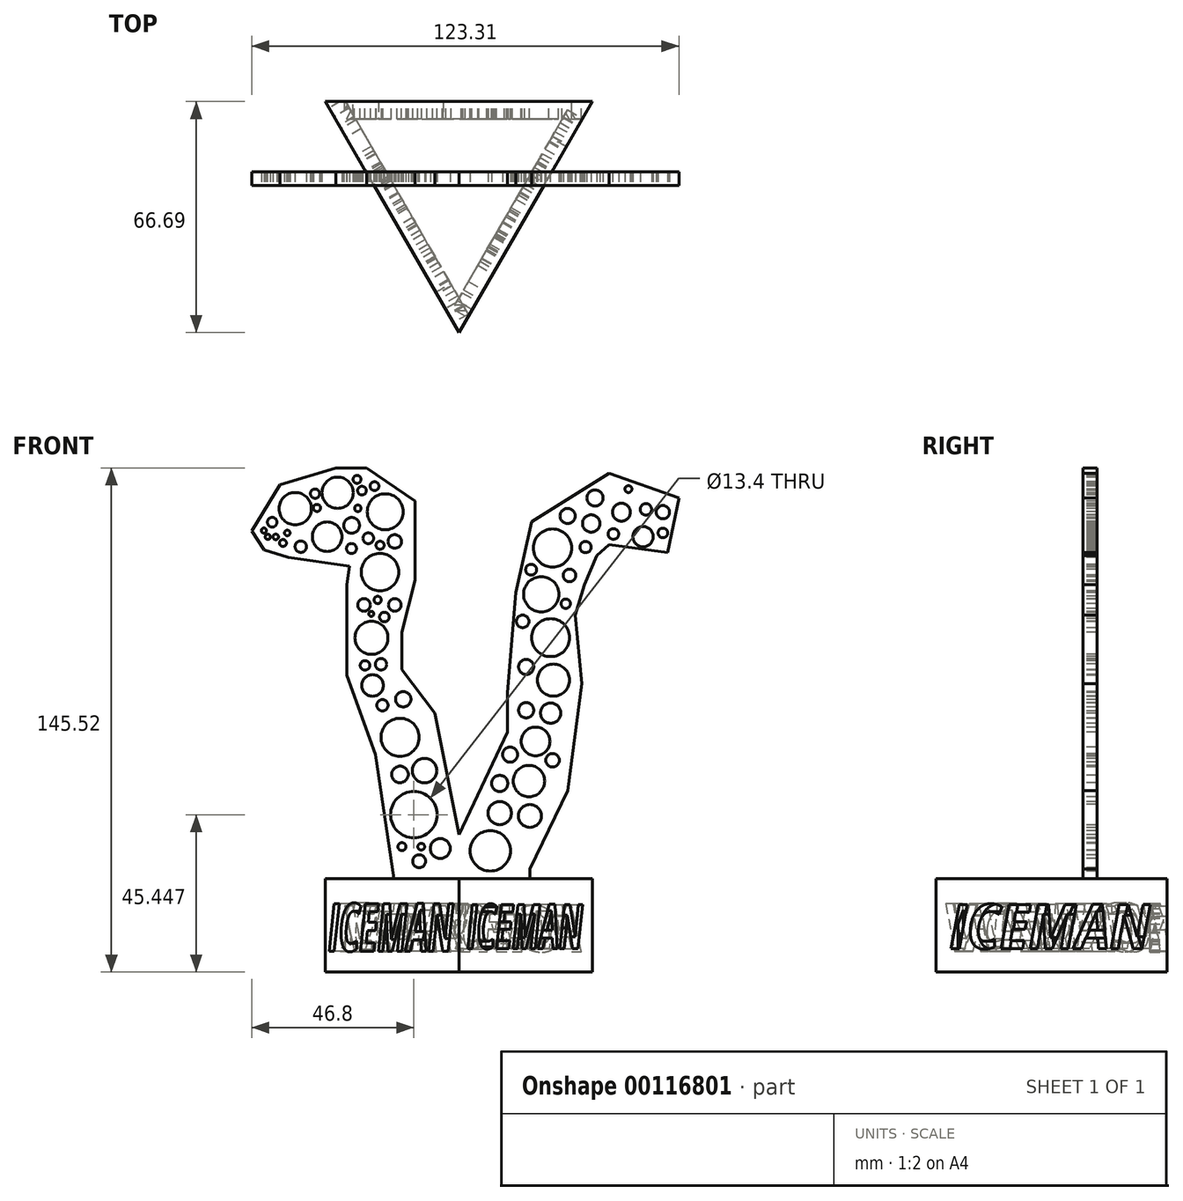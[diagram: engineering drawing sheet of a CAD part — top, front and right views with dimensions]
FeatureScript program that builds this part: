
annotation { "Feature Type Name" : "Feature", "Feature Type Description" : "" }
export const myFeature = defineFeature(function(context is Context, id is Id, definition is map)
    precondition{}
    {
        {
            var Q0;
            Q0=qCreatedBy(makeId("Top.planeOp"),FACE);
            var sketch = newSketch(context, id + "F0", { "sketchPlane" : qUnion([Q0])});
            skCircle(sketch, "E0.cCircle", {"center": v(0, 0) * mm, "radius": 22.23 * mm, "construction": true});
            skLineSegment(sketch, "E0.0", {"start": v(-38.5, 22.23) * mm, "end": v(38.5, 22.23) * mm});
            skLineSegment(sketch, "E0.1", {"start": v(38.5, 22.23) * mm, "end": v(0, -44.46) * mm});
            skLineSegment(sketch, "E0.2", {"start": v(0, -44.46) * mm, "end": v(-38.5, 22.23) * mm});
            skPoint(sketch, "E0.0.midPoint", {"position": v(0, 22.23) * mm});
            skSolve(sketch);
        }
        {
            var Q0;
            Q0 = qSketchRegion(id + "F0", true);
            extrude(context, id + "F1", {"entities" : qUnion([Q0]), "depth" : 27 * mm});
        }
        {
            var Q0;
            Q0=makeQuery(id+"F1.opExtrude","SWEPT_FACE",FACE,{"disambiguationData":[OSD([sQuery(id+"F0.wireOp",EDGE,"E0.0")])]});
            var sketch = newSketch(context, id + "F2", { "sketchPlane" : qUnion([Q0])});
            skText(sketch, "E1", { "text": "ICEMAN", "fontName": "OpenSans-BoldItalic.ttf"});
            skLineSegment(sketch, "E2", {"start": v(0, 35.53) * mm, "end": v(0, -12.2) * mm, "construction": true});
            skPoint(sketch, "E2.endSnap0", {"position": v(0, 27) * mm});
            const initialGuessF2  = {"E1": [-0.03582, 0.00594, 1, 0, 0.01323]};
            skSetInitialGuess(sketch, initialGuessF2);
            skSolve(sketch);
        }
        {
            var Q0;
            Q0 = qSketchRegion(id + "F2", true);
            extrude(context, id + "F3", {"entities" : qUnion([Q0]), "operationType" : NewBodyOperationType.REMOVE, "oppositeDirection" : true, "depth" : 5 * mm});
        }
        {
            var Q0;
            Q0=makeQuery(id+"F1.opExtrude","SWEPT_FACE",FACE,{"disambiguationData":[OSD([sQuery(id+"F0.wireOp",EDGE,"E0.1")])]});
            var sketch = newSketch(context, id + "F4", { "sketchPlane" : qUnion([Q0])});
            skText(sketch, "E3", { "text": "ICEMAN", "fontName": "OpenSans-BoldItalic.ttf"});
            const initialGuessF4  = {"E3": [-0.0339, 0.0068, 1, 0, 0.01285]};
            skSetInitialGuess(sketch, initialGuessF4);
            skSolve(sketch);
        }
        {
            var Q0;
            Q0 = qSketchRegion(id + "F4", true);
            extrude(context, id + "F5", {"entities" : qUnion([Q0]), "operationType" : NewBodyOperationType.REMOVE, "oppositeDirection" : true, "depth" : 5 * mm});
        }
        {
            var Q0;
            Q0=makeQuery(id+"F1.opExtrude","SWEPT_FACE",FACE,{"disambiguationData":[OSD([sQuery(id+"F0.wireOp",EDGE,"E0.2")])]});
            var sketch = newSketch(context, id + "F6", { "sketchPlane" : qUnion([Q0])});
            skText(sketch, "E4", { "text": "ICEMAN", "fontName": "OpenSans-BoldItalic.ttf"});
            const initialGuessF6  = {"E4": [-0.03687, 0.00604, 1, 0, 0.01387]};
            skSetInitialGuess(sketch, initialGuessF6);
            skSolve(sketch);
        }
        {
            var Q0;
            Q0 = qSketchRegion(id + "F6", true);
            var Q1;
            Q1 = qConstructionFilter(qBodyType(qCreatedBy(id + "F6" ,EDGE), BodyType.WIRE), ConstructionObject.NO);
            extrude(context, id + "F7", {"entities" : qUnion([Q0]), "operationType" : NewBodyOperationType.REMOVE, "surfaceEntities" : qUnion([Q1]), "oppositeDirection" : true, "depth" : 5 * mm});
        }
        {
            var Q0;
            Q0=makeQuery(id+"F1.opExtrude","CAP_FACE",FACE,{"disambiguationData":[OSD([sQuery(id+"F0.wireOp",EDGE,"E0.0"),sQuery(id+"F0.wireOp",EDGE,"E0.1"),sQuery(id+"F0.wireOp",EDGE,"E0.2")])],"isStart":false});
            var sketch = newSketch(context, id + "F8", { "sketchPlane" : qUnion([Q0])});
            skLineSegment(sketch, "E5.bottom", {"start": v(63.5, 2) * mm, "end": v(-63.5, 2) * mm});
            skLineSegment(sketch, "E5.top", {"start": v(63.5, -2) * mm, "end": v(-63.5, -2) * mm});
            skLineSegment(sketch, "E5.left", {"start": v(63.5, 2) * mm, "end": v(63.5, -2) * mm});
            skLineSegment(sketch, "E5.right", {"start": v(-63.5, 2) * mm, "end": v(-63.5, -2) * mm});
            skPoint(sketch, "E5.middle", {"position": v(0, 0) * mm});
            skSolve(sketch);
        }
        {
            var Q0;
            {var subQ0=sQuery(id+"F8.wireOp",EDGE,"E5.bottom");var subQ1=makeQuery(id+"F1.opExtrude","CAP_EDGE",EDGE,{"disambiguationData":[OSD([sQuery(id+"F0.wireOp",EDGE,"E0.1")])],"isStart":false});var subQ2=makeQuery(id+"F8.imprint","INTERSECT",VERTEX,{"derivedFrom":[subQ1,subQ0]});Q0=makeQuery(id+"F8.imprint","IMPRINT",FACE,{"disambiguationData":[TD([[makeQuery(id+"F8.imprint","IMPRINT",EDGE,{"disambiguationData":[TD([[subQ2,-1.0]])],"derivedFrom":subQ0}),1.0]])]});}
            var Q1;
            {var subQ0=sQuery(id+"F8.wireOp",EDGE,"E5.right");Q1=makeQuery(id+"F8.imprint","IMPRINT",FACE,{"disambiguationData":[TD([[makeQuery(id+"F8.imprint","IMPRINT",EDGE,{"derivedFrom":subQ0}),1.0]])]});}
            var Q2;
            {var subQ0=sQuery(id+"F8.wireOp",EDGE,"E5.left");Q2=makeQuery(id+"F8.imprint","IMPRINT",FACE,{"disambiguationData":[TD([[makeQuery(id+"F8.imprint","IMPRINT",EDGE,{"derivedFrom":subQ0}),-1.0]])]});}
            extrude(context, id + "F9", {"entities" : qUnion([Q0, Q1, Q2]), "operationType" : NewBodyOperationType.ADD, "depth" : 127 * mm});
        }
        {
            var Q0;
            Q0=makeQuery(id+"F9.opExtrude","SWEPT_FACE",FACE,{"disambiguationData":[OSD([sQuery(id+"F8.wireOp",EDGE,"E5.top")])]});
            var sketch = newSketch(context, id + "F10", { "sketchPlane" : qUnion([Q0])});
            skCircle(sketch, "E6", {"center": v(-50.78, 123.83) * mm, "radius": 1 * mm});
            skCircle(sketch, "E7", {"center": v(48.93, 139.4) * mm, "radius": 1 * mm});
            skCircle(sketch, "E8", {"center": v(-47.23, 133.75) * mm, "radius": 4.66 * mm});
            skCircle(sketch, "E9", {"center": v(-35, 138.33) * mm, "radius": 4.51 * mm});
            skCircle(sketch, "E10", {"center": v(-21.26, 132.83) * mm, "radius": 5.2 * mm});
            skCircle(sketch, "E11", {"center": v(-22.79, 115.42) * mm, "radius": 5.4 * mm});
            skCircle(sketch, "E12", {"center": v(-25.23, 96.47) * mm, "radius": 4.77 * mm});
            skCircle(sketch, "E13", {"center": v(-16.98, 67.75) * mm, "radius": 5.5 * mm});
            skCircle(sketch, "E14", {"center": v(-13.01, 45.45) * mm, "radius": 6.7 * mm});
            skCircle(sketch, "E15", {"center": v(-5.37, 35.67) * mm, "radius": 2.88 * mm});
            skCircle(sketch, "E16", {"center": v(-11.48, 32) * mm, "radius": 1.86 * mm});
            skCircle(sketch, "E17", {"center": v(-16.98, 57.06) * mm, "radius": 2.39 * mm});
            skCircle(sketch, "E18", {"center": v(-16.07, 78.75) * mm, "radius": 2.22 * mm});
            skCircle(sketch, "E19", {"center": v(-24.93, 82.72) * mm, "radius": 3.12 * mm});
            skCircle(sketch, "E20", {"center": v(-27.37, 105.95) * mm, "radius": 1.83 * mm});
            skCircle(sketch, "E21", {"center": v(-18.51, 105.95) * mm, "radius": 1.83 * mm});
            skCircle(sketch, "E22", {"center": v(-22.48, 88.83) * mm, "radius": 1.65 * mm});
            skCircle(sketch, "E23", {"center": v(-26.15, 125.2) * mm, "radius": 1.56 * mm});
            skCircle(sketch, "E24", {"center": v(-18.51, 124.28) * mm, "radius": 1.96 * mm});
            skCircle(sketch, "E25", {"center": v(-27.98, 138.94) * mm, "radius": 1.26 * mm});
            skCircle(sketch, "E26", {"center": v(-29.16, 133.83) * mm, "radius": 0.94 * mm});
            skCircle(sketch, "E27", {"center": v(-40.95, 133.95) * mm, "radius": 1.04 * mm});
            skCircle(sketch, "E28", {"center": v(-41.52, 138.07) * mm, "radius": 1.34 * mm});
            skCircle(sketch, "E29", {"center": v(-53.89, 129.83) * mm, "radius": 1.4 * mm});
            skCircle(sketch, "E30", {"center": v(-49.54, 126.74) * mm, "radius": 0.8 * mm});
            skCircle(sketch, "E31", {"center": v(-55.14, 125.6) * mm, "radius": 0.77 * mm});
            skCircle(sketch, "E32", {"center": v(-52.86, 125.6) * mm, "radius": 0.8 * mm});
            skCircle(sketch, "E33", {"center": v(-56.29, 127.42) * mm, "radius": 0.73 * mm});
            skCircle(sketch, "E34", {"center": v(-24.36, 140.24) * mm, "radius": 1.28 * mm});
            skCircle(sketch, "E35", {"center": v(-29.4, 142.19) * mm, "radius": 1.14 * mm});
            skCircle(sketch, "E36", {"center": v(-22.76, 123.19) * mm, "radius": 1.18 * mm});
            skCircle(sketch, "E37", {"center": v(-23.44, 107.4) * mm, "radius": 1.06 * mm});
            skCircle(sketch, "E38", {"center": v(-21.5, 102.47) * mm, "radius": 1.4 * mm});
            skCircle(sketch, "E39", {"center": v(-25.27, 103.39) * mm, "radius": 0.73 * mm});
            skCircle(sketch, "E40", {"center": v(-27.1, 88.5) * mm, "radius": 1.38 * mm});
            skCircle(sketch, "E41", {"center": v(-22.07, 77.01) * mm, "radius": 1.63 * mm});
            skCircle(sketch, "E42", {"center": v(-9.9, 58.14) * mm, "radius": 3.54 * mm});
            skCircle(sketch, "E43", {"center": v(-16.45, 36.2) * mm, "radius": 1.15 * mm});
            skCircle(sketch, "E44", {"center": v(-10.86, 36.2) * mm, "radius": 0.98 * mm});
            skCircle(sketch, "E45", {"center": v(9.06, 35) * mm, "radius": 5.82 * mm});
            skCircle(sketch, "E46", {"center": v(11.79, 45.89) * mm, "radius": 3.37 * mm});
            skCircle(sketch, "E47", {"center": v(20.5, 45.07) * mm, "radius": 3.31 * mm});
            skCircle(sketch, "E48", {"center": v(20.22, 55.14) * mm, "radius": 4.53 * mm});
            skCircle(sketch, "E49", {"center": v(22.13, 66.58) * mm, "radius": 4.15 * mm});
            skCircle(sketch, "E50", {"center": v(26.49, 74.74) * mm, "radius": 2.93 * mm});
            skCircle(sketch, "E51", {"center": v(27.3, 84.27) * mm, "radius": 4.64 * mm});
            skCircle(sketch, "E52", {"center": v(26.49, 96.52) * mm, "radius": 5.47 * mm});
            skCircle(sketch, "E53", {"center": v(19.4, 75.56) * mm, "radius": 2.2 * mm});
            skCircle(sketch, "E54", {"center": v(19.4, 88.08) * mm, "radius": 2.18 * mm});
            skCircle(sketch, "E55", {"center": v(23.76, 109.04) * mm, "radius": 5.09 * mm});
            skCircle(sketch, "E56", {"center": v(27.03, 122.38) * mm, "radius": 5.51 * mm});
            skCircle(sketch, "E57", {"center": v(38.2, 129.46) * mm, "radius": 2.5 * mm});
            skCircle(sketch, "E58", {"center": v(31.39, 131.64) * mm, "radius": 2.2 * mm});
            skCircle(sketch, "E59", {"center": v(39.28, 136.8) * mm, "radius": 2.34 * mm});
            skCircle(sketch, "E60", {"center": v(46.9, 132.72) * mm, "radius": 2.58 * mm});
            skCircle(sketch, "E61", {"center": v(53.16, 125.65) * mm, "radius": 2.93 * mm});
            skCircle(sketch, "E62", {"center": v(53.98, 133.54) * mm, "radius": 1.66 * mm});
            skCircle(sketch, "E63", {"center": v(58.88, 132.72) * mm, "radius": 1.92 * mm});
            skCircle(sketch, "E64", {"center": v(58.88, 126.74) * mm, "radius": 1.39 * mm});
            skCircle(sketch, "E65", {"center": v(31.93, 114.49) * mm, "radius": 1.83 * mm});
            skCircle(sketch, "E66", {"center": v(30.84, 106.32) * mm, "radius": 1.36 * mm});
            skCircle(sketch, "E67", {"center": v(36.56, 122.65) * mm, "radius": 1.63 * mm});
            skLineSegment(sketch, "E68", {"start": v(0, 39.63) * mm, "end": v(-7, 74.74) * mm});
            skLineSegment(sketch, "E69", {"start": v(-7, 74.74) * mm, "end": v(-16.52, 87.27) * mm});
            skLineSegment(sketch, "E70", {"start": v(-16.52, 87.27) * mm, "end": v(-16.52, 98.15) * mm});
            skLineSegment(sketch, "E71", {"start": v(-16.52, 98.15) * mm, "end": v(-12.71, 113.13) * mm});
            skLineSegment(sketch, "E72", {"start": v(-12.71, 113.13) * mm, "end": v(-12.71, 136) * mm});
            skLineSegment(sketch, "E73", {"start": v(-12.71, 136) * mm, "end": v(-26.6, 145.52) * mm});
            skLineSegment(sketch, "E74", {"start": v(-26.6, 145.52) * mm, "end": v(-35.58, 145.52) * mm});
            skLineSegment(sketch, "E75", {"start": v(-35.58, 145.52) * mm, "end": v(-51.64, 140.62) * mm});
            skLineSegment(sketch, "E76", {"start": v(-51.64, 140.62) * mm, "end": v(-59.8, 127.28) * mm});
            skLineSegment(sketch, "E77", {"start": v(-59.8, 127.28) * mm, "end": v(-56.27, 121.84) * mm});
            skLineSegment(sketch, "E78", {"start": v(-56.27, 121.84) * mm, "end": v(-49.19, 119.66) * mm});
            skLineSegment(sketch, "E79", {"start": v(-31.54, 117.1) * mm, "end": v(-32.31, 111.76) * mm});
            skLineSegment(sketch, "E80", {"start": v(-32.31, 111.76) * mm, "end": v(-32.31, 85.63) * mm});
            skLineSegment(sketch, "E81", {"start": v(-32.31, 85.63) * mm, "end": v(-24.15, 62.77) * mm});
            skLineSegment(sketch, "E82", {"start": v(-24.15, 62.77) * mm, "end": v(-18.7, 27) * mm});
            skLineSegment(sketch, "E83", {"start": v(0, 39.63) * mm, "end": v(14.01, 69.28) * mm});
            skLineSegment(sketch, "E84", {"start": v(14.01, 69.28) * mm, "end": v(14.01, 80.73) * mm});
            skLineSegment(sketch, "E85", {"start": v(14.01, 80.73) * mm, "end": v(16.41, 109.59) * mm});
            skLineSegment(sketch, "E86", {"start": v(16.41, 109.59) * mm, "end": v(21.04, 130) * mm});
            skLineSegment(sketch, "E87", {"start": v(21.04, 130) * mm, "end": v(43.36, 143.89) * mm});
            skLineSegment(sketch, "E88", {"start": v(43.36, 143.89) * mm, "end": v(63.5, 136.8) * mm});
            skLineSegment(sketch, "E89", {"start": v(63.5, 136.8) * mm, "end": v(60.24, 121.02) * mm});
            skLineSegment(sketch, "E90", {"start": v(60.24, 121.02) * mm, "end": v(43.34, 123.36) * mm});
            skLineSegment(sketch, "E91", {"start": v(43.34, 123.36) * mm, "end": v(39.82, 120.2) * mm});
            skLineSegment(sketch, "E92", {"start": v(39.82, 120.2) * mm, "end": v(36.29, 111.76) * mm});
            skLineSegment(sketch, "E93", {"start": v(36.29, 111.76) * mm, "end": v(33.56, 103.05) * mm});
            skLineSegment(sketch, "E94", {"start": v(33.56, 103.05) * mm, "end": v(35.47, 83.18) * mm});
            skLineSegment(sketch, "E95", {"start": v(35.47, 83.18) * mm, "end": v(31.39, 52.42) * mm});
            skLineSegment(sketch, "E96", {"start": v(31.39, 52.42) * mm, "end": v(20.5, 29.83) * mm});
            skCircle(sketch, "E97", {"center": v(11.79, 54.45) * mm, "radius": 2.34 * mm});
            skPoint(sketch, "E97.centerSnap0", {"position": v(7, 54.45) * mm});
            skCircle(sketch, "E98", {"center": v(14.78, 62.77) * mm, "radius": 2.18 * mm});
            skCircle(sketch, "E99", {"center": v(27.03, 61.13) * mm, "radius": 1.96 * mm});
            skLineSegment(sketch, "E100", {"start": v(-49.19, 119.66) * mm, "end": v(-31.54, 117.1) * mm});
            skCircle(sketch, "E101", {"center": v(-38.03, 125.65) * mm, "radius": 4.26 * mm});
            skCircle(sketch, "E102", {"center": v(-30.95, 128.91) * mm, "radius": 2.27 * mm});
            skCircle(sketch, "E103", {"center": v(-31, 122.23) * mm, "radius": 1.45 * mm});
            skCircle(sketch, "E104", {"center": v(-45.63, 122.77) * mm, "radius": 1.65 * mm});
            skCircle(sketch, "E105", {"center": v(20.84, 116.12) * mm, "radius": 1.58 * mm});
            skCircle(sketch, "E106", {"center": v(18.41, 101.2) * mm, "radius": 1.82 * mm});
            skCircle(sketch, "E107", {"center": v(44.6, 126.43) * mm, "radius": 1.53 * mm});
            skLineSegment(sketch, "E108", {"start": v(20.5, 29.83) * mm, "end": v(20.5, 27) * mm});
            skPoint(sketch, "E108.endSnap0", {"position": v(0, 27) * mm});
            skSolve(sketch);
        }
        {
            var Q0;
            Q0=makeQuery(id+"F10.imprint","IMPRINT",FACE,{"disambiguationData":[TD([[makeQuery(id+"F10.imprint","IMPRINT",EDGE,{"derivedFrom":sQuery(id+"F10.wireOp",EDGE,"E68")}),-1.0]])]});
            var Q1;
            {var subQ13=sQuery(id+"F10.wireOp",EDGE,"E89");Q1=makeQuery(id+"F10.imprint","IMPRINT",FACE,{"disambiguationData":[TD([[makeQuery(id+"F10.imprint","IMPRINT",EDGE,{"derivedFrom":subQ13}),1.0]])]});}
            var Q2;
            Q2=makeQuery(id+"F10.imprint","IMPRINT",FACE,{"disambiguationData":[TD([[makeQuery(id+"F10.imprint","IMPRINT",EDGE,{"derivedFrom":sQuery(id+"F10.wireOp",EDGE,"E101")}),1.0]])]});
            var Q3;
            Q3=makeQuery(id+"F10.imprint","IMPRINT",FACE,{"disambiguationData":[TD([[makeQuery(id+"F10.imprint","IMPRINT",EDGE,{"derivedFrom":sQuery(id+"F10.wireOp",EDGE,"E11")}),1.0]])]});
            var Q4;
            Q4=makeQuery(id+"F10.imprint","IMPRINT",FACE,{"disambiguationData":[TD([[makeQuery(id+"F10.imprint","IMPRINT",EDGE,{"derivedFrom":sQuery(id+"F10.wireOp",EDGE,"E9")}),1.0]])]});
            var Q5;
            Q5=makeQuery(id+"F10.imprint","IMPRINT",FACE,{"disambiguationData":[TD([[makeQuery(id+"F10.imprint","IMPRINT",EDGE,{"derivedFrom":sQuery(id+"F10.wireOp",EDGE,"E8")}),1.0]])]});
            var Q6;
            Q6=makeQuery(id+"F10.imprint","IMPRINT",FACE,{"disambiguationData":[TD([[makeQuery(id+"F10.imprint","IMPRINT",EDGE,{"derivedFrom":sQuery(id+"F10.wireOp",EDGE,"E29")}),1.0]])]});
            var Q7;
            Q7=makeQuery(id+"F10.imprint","IMPRINT",FACE,{"disambiguationData":[TD([[makeQuery(id+"F10.imprint","IMPRINT",EDGE,{"derivedFrom":sQuery(id+"F10.wireOp",EDGE,"E33")}),1.0]])]});
            var Q8;
            Q8=makeQuery(id+"F10.imprint","IMPRINT",FACE,{"disambiguationData":[TD([[makeQuery(id+"F10.imprint","IMPRINT",EDGE,{"derivedFrom":sQuery(id+"F10.wireOp",EDGE,"E31")}),1.0]])]});
            var Q9;
            Q9=makeQuery(id+"F10.imprint","IMPRINT",FACE,{"disambiguationData":[TD([[makeQuery(id+"F10.imprint","IMPRINT",EDGE,{"derivedFrom":sQuery(id+"F10.wireOp",EDGE,"E32")}),1.0]])]});
            var Q10;
            Q10=makeQuery(id+"F10.imprint","IMPRINT",FACE,{"disambiguationData":[TD([[makeQuery(id+"F10.imprint","IMPRINT",EDGE,{"derivedFrom":sQuery(id+"F10.wireOp",EDGE,"E6")}),1.0]])]});
            var Q11;
            Q11=makeQuery(id+"F10.imprint","IMPRINT",FACE,{"disambiguationData":[TD([[makeQuery(id+"F10.imprint","IMPRINT",EDGE,{"derivedFrom":sQuery(id+"F10.wireOp",EDGE,"E30")}),1.0]])]});
            var Q12;
            Q12=makeQuery(id+"F10.imprint","IMPRINT",FACE,{"disambiguationData":[TD([[makeQuery(id+"F10.imprint","IMPRINT",EDGE,{"derivedFrom":sQuery(id+"F10.wireOp",EDGE,"E104")}),1.0]])]});
            var Q13;
            Q13=makeQuery(id+"F10.imprint","IMPRINT",FACE,{"disambiguationData":[TD([[makeQuery(id+"F10.imprint","IMPRINT",EDGE,{"derivedFrom":sQuery(id+"F10.wireOp",EDGE,"E102")}),1.0]])]});
            var Q14;
            Q14=makeQuery(id+"F10.imprint","IMPRINT",FACE,{"disambiguationData":[TD([[makeQuery(id+"F10.imprint","IMPRINT",EDGE,{"derivedFrom":sQuery(id+"F10.wireOp",EDGE,"E27")}),1.0]])]});
            var Q15;
            Q15=makeQuery(id+"F10.imprint","IMPRINT",FACE,{"disambiguationData":[TD([[makeQuery(id+"F10.imprint","IMPRINT",EDGE,{"derivedFrom":sQuery(id+"F10.wireOp",EDGE,"E28")}),1.0]])]});
            var Q16;
            Q16=makeQuery(id+"F10.imprint","IMPRINT",FACE,{"disambiguationData":[TD([[makeQuery(id+"F10.imprint","IMPRINT",EDGE,{"derivedFrom":sQuery(id+"F10.wireOp",EDGE,"E10")}),1.0]])]});
            var Q17;
            Q17=makeQuery(id+"F10.imprint","IMPRINT",FACE,{"disambiguationData":[TD([[makeQuery(id+"F10.imprint","IMPRINT",EDGE,{"derivedFrom":sQuery(id+"F10.wireOp",EDGE,"E26")}),1.0]])]});
            var Q18;
            Q18=makeQuery(id+"F10.imprint","IMPRINT",FACE,{"disambiguationData":[TD([[makeQuery(id+"F10.imprint","IMPRINT",EDGE,{"derivedFrom":sQuery(id+"F10.wireOp",EDGE,"E23")}),1.0]])]});
            var Q19;
            Q19=makeQuery(id+"F10.imprint","IMPRINT",FACE,{"disambiguationData":[TD([[makeQuery(id+"F10.imprint","IMPRINT",EDGE,{"derivedFrom":sQuery(id+"F10.wireOp",EDGE,"E103")}),1.0]])]});
            var Q20;
            Q20=makeQuery(id+"F10.imprint","IMPRINT",FACE,{"disambiguationData":[TD([[makeQuery(id+"F10.imprint","IMPRINT",EDGE,{"derivedFrom":sQuery(id+"F10.wireOp",EDGE,"E36")}),1.0]])]});
            var Q21;
            Q21=makeQuery(id+"F10.imprint","IMPRINT",FACE,{"disambiguationData":[TD([[makeQuery(id+"F10.imprint","IMPRINT",EDGE,{"derivedFrom":sQuery(id+"F10.wireOp",EDGE,"E24")}),1.0]])]});
            var Q22;
            Q22=makeQuery(id+"F10.imprint","IMPRINT",FACE,{"disambiguationData":[TD([[makeQuery(id+"F10.imprint","IMPRINT",EDGE,{"derivedFrom":sQuery(id+"F10.wireOp",EDGE,"E37")}),1.0]])]});
            var Q23;
            Q23=makeQuery(id+"F10.imprint","IMPRINT",FACE,{"disambiguationData":[TD([[makeQuery(id+"F10.imprint","IMPRINT",EDGE,{"derivedFrom":sQuery(id+"F10.wireOp",EDGE,"E20")}),1.0]])]});
            var Q24;
            Q24=makeQuery(id+"F10.imprint","IMPRINT",FACE,{"disambiguationData":[TD([[makeQuery(id+"F10.imprint","IMPRINT",EDGE,{"derivedFrom":sQuery(id+"F10.wireOp",EDGE,"E39")}),1.0]])]});
            var Q25;
            Q25=makeQuery(id+"F10.imprint","IMPRINT",FACE,{"disambiguationData":[TD([[makeQuery(id+"F10.imprint","IMPRINT",EDGE,{"derivedFrom":sQuery(id+"F10.wireOp",EDGE,"E38")}),1.0]])]});
            var Q26;
            Q26=makeQuery(id+"F10.imprint","IMPRINT",FACE,{"disambiguationData":[TD([[makeQuery(id+"F10.imprint","IMPRINT",EDGE,{"derivedFrom":sQuery(id+"F10.wireOp",EDGE,"E21")}),1.0]])]});
            var Q27;
            Q27=makeQuery(id+"F10.imprint","IMPRINT",FACE,{"disambiguationData":[TD([[makeQuery(id+"F10.imprint","IMPRINT",EDGE,{"derivedFrom":sQuery(id+"F10.wireOp",EDGE,"E12")}),1.0]])]});
            var Q28;
            Q28=makeQuery(id+"F10.imprint","IMPRINT",FACE,{"disambiguationData":[TD([[makeQuery(id+"F10.imprint","IMPRINT",EDGE,{"derivedFrom":sQuery(id+"F10.wireOp",EDGE,"E40")}),1.0]])]});
            var Q29;
            Q29=makeQuery(id+"F10.imprint","IMPRINT",FACE,{"disambiguationData":[TD([[makeQuery(id+"F10.imprint","IMPRINT",EDGE,{"derivedFrom":sQuery(id+"F10.wireOp",EDGE,"E22")}),1.0]])]});
            var Q30;
            Q30=makeQuery(id+"F10.imprint","IMPRINT",FACE,{"disambiguationData":[TD([[makeQuery(id+"F10.imprint","IMPRINT",EDGE,{"derivedFrom":sQuery(id+"F10.wireOp",EDGE,"E19")}),1.0]])]});
            var Q31;
            Q31=makeQuery(id+"F10.imprint","IMPRINT",FACE,{"disambiguationData":[TD([[makeQuery(id+"F10.imprint","IMPRINT",EDGE,{"derivedFrom":sQuery(id+"F10.wireOp",EDGE,"E41")}),1.0]])]});
            var Q32;
            Q32=makeQuery(id+"F10.imprint","IMPRINT",FACE,{"disambiguationData":[TD([[makeQuery(id+"F10.imprint","IMPRINT",EDGE,{"derivedFrom":sQuery(id+"F10.wireOp",EDGE,"E18")}),1.0]])]});
            var Q33;
            Q33=makeQuery(id+"F10.imprint","IMPRINT",FACE,{"disambiguationData":[TD([[makeQuery(id+"F10.imprint","IMPRINT",EDGE,{"derivedFrom":sQuery(id+"F10.wireOp",EDGE,"E13")}),1.0]])]});
            var Q34;
            Q34=makeQuery(id+"F10.imprint","IMPRINT",FACE,{"disambiguationData":[TD([[makeQuery(id+"F10.imprint","IMPRINT",EDGE,{"derivedFrom":sQuery(id+"F10.wireOp",EDGE,"E63")}),1.0]])]});
            var Q35;
            Q35=makeQuery(id+"F10.imprint","IMPRINT",FACE,{"disambiguationData":[TD([[makeQuery(id+"F10.imprint","IMPRINT",EDGE,{"derivedFrom":sQuery(id+"F10.wireOp",EDGE,"E60")}),1.0]])]});
            var Q36;
            Q36=makeQuery(id+"F10.imprint","IMPRINT",FACE,{"disambiguationData":[TD([[makeQuery(id+"F10.imprint","IMPRINT",EDGE,{"derivedFrom":sQuery(id+"F10.wireOp",EDGE,"E107")}),1.0]])]});
            var Q37;
            Q37=makeQuery(id+"F10.imprint","IMPRINT",FACE,{"disambiguationData":[TD([[makeQuery(id+"F10.imprint","IMPRINT",EDGE,{"derivedFrom":sQuery(id+"F10.wireOp",EDGE,"E57")}),1.0]])]});
            var Q38;
            Q38=makeQuery(id+"F10.imprint","IMPRINT",FACE,{"disambiguationData":[TD([[makeQuery(id+"F10.imprint","IMPRINT",EDGE,{"derivedFrom":sQuery(id+"F10.wireOp",EDGE,"E58")}),1.0]])]});
            var Q39;
            Q39=makeQuery(id+"F10.imprint","IMPRINT",FACE,{"disambiguationData":[TD([[makeQuery(id+"F10.imprint","IMPRINT",EDGE,{"derivedFrom":sQuery(id+"F10.wireOp",EDGE,"E56")}),1.0]])]});
            var Q40;
            Q40=makeQuery(id+"F10.imprint","IMPRINT",FACE,{"disambiguationData":[TD([[makeQuery(id+"F10.imprint","IMPRINT",EDGE,{"derivedFrom":sQuery(id+"F10.wireOp",EDGE,"E55")}),1.0]])]});
            var Q41;
            Q41=makeQuery(id+"F10.imprint","IMPRINT",FACE,{"disambiguationData":[TD([[makeQuery(id+"F10.imprint","IMPRINT",EDGE,{"derivedFrom":sQuery(id+"F10.wireOp",EDGE,"E105")}),1.0]])]});
            var Q42;
            Q42=makeQuery(id+"F10.imprint","IMPRINT",FACE,{"disambiguationData":[TD([[makeQuery(id+"F10.imprint","IMPRINT",EDGE,{"derivedFrom":sQuery(id+"F10.wireOp",EDGE,"E106")}),1.0]])]});
            var Q43;
            Q43=makeQuery(id+"F10.imprint","IMPRINT",FACE,{"disambiguationData":[TD([[makeQuery(id+"F10.imprint","IMPRINT",EDGE,{"derivedFrom":sQuery(id+"F10.wireOp",EDGE,"E66")}),1.0]])]});
            var Q44;
            Q44=makeQuery(id+"F10.imprint","IMPRINT",FACE,{"disambiguationData":[TD([[makeQuery(id+"F10.imprint","IMPRINT",EDGE,{"derivedFrom":sQuery(id+"F10.wireOp",EDGE,"E65")}),1.0]])]});
            var Q45;
            Q45=makeQuery(id+"F10.imprint","IMPRINT",FACE,{"disambiguationData":[TD([[makeQuery(id+"F10.imprint","IMPRINT",EDGE,{"derivedFrom":sQuery(id+"F10.wireOp",EDGE,"E52")}),1.0]])]});
            var Q46;
            Q46=makeQuery(id+"F10.imprint","IMPRINT",FACE,{"disambiguationData":[TD([[makeQuery(id+"F10.imprint","IMPRINT",EDGE,{"derivedFrom":sQuery(id+"F10.wireOp",EDGE,"E51")}),1.0]])]});
            var Q47;
            Q47=makeQuery(id+"F10.imprint","IMPRINT",FACE,{"disambiguationData":[TD([[makeQuery(id+"F10.imprint","IMPRINT",EDGE,{"derivedFrom":sQuery(id+"F10.wireOp",EDGE,"E54")}),1.0]])]});
            var Q48;
            Q48=makeQuery(id+"F10.imprint","IMPRINT",FACE,{"disambiguationData":[TD([[makeQuery(id+"F10.imprint","IMPRINT",EDGE,{"derivedFrom":sQuery(id+"F10.wireOp",EDGE,"E53")}),1.0]])]});
            var Q49;
            Q49=makeQuery(id+"F10.imprint","IMPRINT",FACE,{"disambiguationData":[TD([[makeQuery(id+"F10.imprint","IMPRINT",EDGE,{"derivedFrom":sQuery(id+"F10.wireOp",EDGE,"E50")}),1.0]])]});
            var Q50;
            Q50=makeQuery(id+"F10.imprint","IMPRINT",FACE,{"disambiguationData":[TD([[makeQuery(id+"F10.imprint","IMPRINT",EDGE,{"derivedFrom":sQuery(id+"F10.wireOp",EDGE,"E49")}),1.0]])]});
            var Q51;
            Q51=makeQuery(id+"F10.imprint","IMPRINT",FACE,{"disambiguationData":[TD([[makeQuery(id+"F10.imprint","IMPRINT",EDGE,{"derivedFrom":sQuery(id+"F10.wireOp",EDGE,"E98")}),1.0]])]});
            var Q52;
            Q52=makeQuery(id+"F10.imprint","IMPRINT",FACE,{"disambiguationData":[TD([[makeQuery(id+"F10.imprint","IMPRINT",EDGE,{"derivedFrom":sQuery(id+"F10.wireOp",EDGE,"E48")}),1.0]])]});
            var Q53;
            Q53=makeQuery(id+"F10.imprint","IMPRINT",FACE,{"disambiguationData":[TD([[makeQuery(id+"F10.imprint","IMPRINT",EDGE,{"derivedFrom":sQuery(id+"F10.wireOp",EDGE,"E99")}),1.0]])]});
            var Q54;
            Q54=makeQuery(id+"F10.imprint","IMPRINT",FACE,{"disambiguationData":[TD([[makeQuery(id+"F10.imprint","IMPRINT",EDGE,{"derivedFrom":sQuery(id+"F10.wireOp",EDGE,"E47")}),1.0]])]});
            var Q55;
            Q55=makeQuery(id+"F10.imprint","IMPRINT",FACE,{"disambiguationData":[TD([[makeQuery(id+"F10.imprint","IMPRINT",EDGE,{"derivedFrom":sQuery(id+"F10.wireOp",EDGE,"E46")}),1.0]])]});
            var Q56;
            Q56=makeQuery(id+"F10.imprint","IMPRINT",FACE,{"disambiguationData":[TD([[makeQuery(id+"F10.imprint","IMPRINT",EDGE,{"derivedFrom":sQuery(id+"F10.wireOp",EDGE,"E97")}),1.0]])]});
            var Q57;
            Q57=makeQuery(id+"F10.imprint","IMPRINT",FACE,{"disambiguationData":[TD([[makeQuery(id+"F10.imprint","IMPRINT",EDGE,{"derivedFrom":sQuery(id+"F10.wireOp",EDGE,"E45")}),1.0]])]});
            var Q58;
            Q58=makeQuery(id+"F10.imprint","IMPRINT",FACE,{"disambiguationData":[TD([[makeQuery(id+"F10.imprint","IMPRINT",EDGE,{"derivedFrom":sQuery(id+"F10.wireOp",EDGE,"E16")}),1.0]])]});
            var Q59;
            Q59=makeQuery(id+"F10.imprint","IMPRINT",FACE,{"disambiguationData":[TD([[makeQuery(id+"F10.imprint","IMPRINT",EDGE,{"derivedFrom":sQuery(id+"F10.wireOp",EDGE,"E15")}),1.0]])]});
            var Q60;
            Q60=makeQuery(id+"F10.imprint","IMPRINT",FACE,{"disambiguationData":[TD([[makeQuery(id+"F10.imprint","IMPRINT",EDGE,{"derivedFrom":sQuery(id+"F10.wireOp",EDGE,"E44")}),1.0]])]});
            var Q61;
            Q61=makeQuery(id+"F10.imprint","IMPRINT",FACE,{"disambiguationData":[TD([[makeQuery(id+"F10.imprint","IMPRINT",EDGE,{"derivedFrom":sQuery(id+"F10.wireOp",EDGE,"E43")}),1.0]])]});
            var Q62;
            Q62=makeQuery(id+"F10.imprint","IMPRINT",FACE,{"disambiguationData":[TD([[makeQuery(id+"F10.imprint","IMPRINT",EDGE,{"derivedFrom":sQuery(id+"F10.wireOp",EDGE,"E14")}),1.0]])]});
            var Q63;
            Q63=makeQuery(id+"F10.imprint","IMPRINT",FACE,{"disambiguationData":[TD([[makeQuery(id+"F10.imprint","IMPRINT",EDGE,{"derivedFrom":sQuery(id+"F10.wireOp",EDGE,"E17")}),1.0]])]});
            var Q64;
            Q64=makeQuery(id+"F10.imprint","IMPRINT",FACE,{"disambiguationData":[TD([[makeQuery(id+"F10.imprint","IMPRINT",EDGE,{"derivedFrom":sQuery(id+"F10.wireOp",EDGE,"E42")}),1.0]])]});
            var Q65;
            Q65=makeQuery(id+"F10.imprint","IMPRINT",FACE,{"disambiguationData":[TD([[makeQuery(id+"F10.imprint","IMPRINT",EDGE,{"derivedFrom":sQuery(id+"F10.wireOp",EDGE,"E59")}),1.0]])]});
            var Q66;
            Q66=makeQuery(id+"F10.imprint","IMPRINT",FACE,{"disambiguationData":[TD([[makeQuery(id+"F10.imprint","IMPRINT",EDGE,{"derivedFrom":sQuery(id+"F10.wireOp",EDGE,"E7")}),1.0]])]});
            var Q67;
            Q67=makeQuery(id+"F10.imprint","IMPRINT",FACE,{"disambiguationData":[TD([[makeQuery(id+"F10.imprint","IMPRINT",EDGE,{"derivedFrom":sQuery(id+"F10.wireOp",EDGE,"E62")}),1.0]])]});
            var Q68;
            Q68=makeQuery(id+"F10.imprint","IMPRINT",FACE,{"disambiguationData":[TD([[makeQuery(id+"F10.imprint","IMPRINT",EDGE,{"derivedFrom":sQuery(id+"F10.wireOp",EDGE,"E61")}),1.0]])]});
            var Q69;
            Q69=makeQuery(id+"F10.imprint","IMPRINT",FACE,{"disambiguationData":[TD([[makeQuery(id+"F10.imprint","IMPRINT",EDGE,{"derivedFrom":sQuery(id+"F10.wireOp",EDGE,"E64")}),1.0]])]});
            var Q70;
            Q70=makeQuery(id+"F10.imprint","IMPRINT",FACE,{"disambiguationData":[TD([[makeQuery(id+"F10.imprint","IMPRINT",EDGE,{"derivedFrom":sQuery(id+"F10.wireOp",EDGE,"E67")}),1.0]])]});
            var Q71;
            Q71=makeQuery(id+"F10.imprint","IMPRINT",FACE,{"disambiguationData":[TD([[makeQuery(id+"F10.imprint","IMPRINT",EDGE,{"derivedFrom":sQuery(id+"F10.wireOp",EDGE,"E35")}),1.0]])]});
            var Q72;
            Q72=makeQuery(id+"F10.imprint","IMPRINT",FACE,{"disambiguationData":[TD([[makeQuery(id+"F10.imprint","IMPRINT",EDGE,{"derivedFrom":sQuery(id+"F10.wireOp",EDGE,"E25")}),1.0]])]});
            var Q73;
            Q73=makeQuery(id+"F10.imprint","IMPRINT",FACE,{"disambiguationData":[TD([[makeQuery(id+"F10.imprint","IMPRINT",EDGE,{"derivedFrom":sQuery(id+"F10.wireOp",EDGE,"E34")}),1.0]])]});
            extrude(context, id + "F11", {"entities" : qUnion([Q0, Q1, Q2, Q3, Q4, Q5, Q6, Q7, Q8, Q9, Q10, Q11, Q12, Q13, Q14, Q15, Q16, Q17, Q18, Q19, Q20, Q21, Q22, Q23, Q24, Q25, Q26, Q27, Q28, Q29, Q30, Q31, Q32, Q33, Q34, Q35, Q36, Q37, Q38, Q39, Q40, Q41, Q42, Q43, Q44, Q45, Q46, Q47, Q48, Q49, Q50, Q51, Q52, Q53, Q54, Q55, Q56, Q57, Q58, Q59, Q60, Q61, Q62, Q63, Q64, Q65, Q66, Q67, Q68, Q69, Q70, Q71, Q72, Q73]), "operationType" : NewBodyOperationType.REMOVE, "endBound" : BoundingType.THROUGH_ALL, "oppositeDirection" : true, "depth" : 25 * mm});
        }
    });
